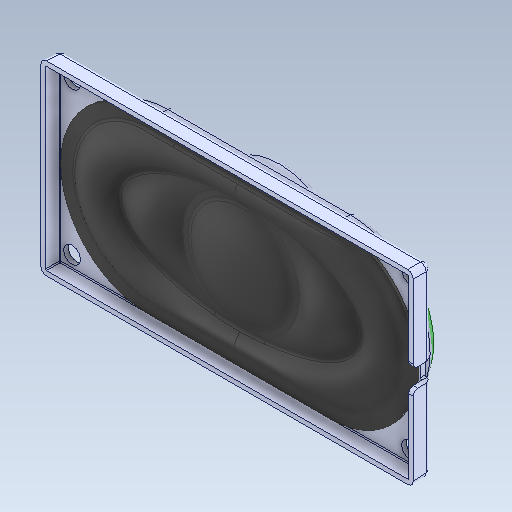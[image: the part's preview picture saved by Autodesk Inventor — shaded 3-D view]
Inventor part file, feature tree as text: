
AUTODESK INVENTOR PART (.ipt)
format: ipt  version: 2020.3 (Build 243373000, 373)  size: 1,304,576 bytes
history: native  units: in
note: dims shown in document units (in); Inventor stores cm internally (conversion verified against a paired STEP export)
features: other x6, fillet x1, thicken_offset x1
ambient origin geometry x8: Origin, YZ Plane, XZ Plane, XY Plane, X Axis, Y Axis, Z Axis, Center Point
bodies: Solid1 (feature_tree), Solid2 (feature_tree), Solid3 (feature_tree), Solid4 (feature_tree), Solid5 (feature_tree), Solid6 (feature_tree), Solid7 (feature_tree), Solid8 (feature_tree)
feature tree (8):
  other  "Decal[1]"
  other  "Decal[2]"
  other  "Decal[3]"
  other  "Decal[4]"
  fillet  "Fillet2"  [1 undecoded]
  other  "Magnet fillets"
  thicken_offset  "Thicken2"
  other  "PCB"
note: 1 required parameter value undecoded (feature->parameter linkage not recoverable at this tier; creation-order binding heuristic only, values carry confidence <= 0.55)
